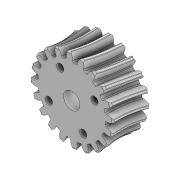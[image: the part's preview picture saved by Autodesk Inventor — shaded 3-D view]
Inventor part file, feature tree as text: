
AUTODESK INVENTOR PART (.ipt)
format: ipt  version: 2022 (Build 260153000, 153)  size: 1,369,600 bytes
history: native  units: in
note: dims shown in document units (in); Inventor stores cm internally (conversion verified against a paired STEP export)
features: extrude x3, sketch x3, pattern_circular x1, projected_geometry x1, other x1
ambient origin geometry x8: Origin, YZ Plane, XZ Plane, XY Plane, X Axis, Y Axis, Z Axis, Center Point
bodies: Solid1 (feature_tree)
feature tree (9):
  extrude  "Extrusion1"  Depth=0.0787in
  extrude  "Extrusion2"  Depth=3.937in TaperAngle=0.0deg
  pattern_circular  "Circular Pattern1"  Count=4 Angle=360.0deg
  extrude  "Extrusion4"  Depth=0.3937in TaperAngle=0.0deg
  sketch  "Sketch1"  dims[d0=3.937in d1=0.0in d2=0.0787in]
  projected_geometry  "Projected Loop1"
  sketch  "Sketch2"  dims[d3=0.2756in d4=3.937in d5=0.0in d6=1.5748in d7=360.0deg]
  sketch  "Sketch4"  dims[d13=0.1772in d14=0.3937in d15=0.0in]
  other  "Boss-Extrude1"
